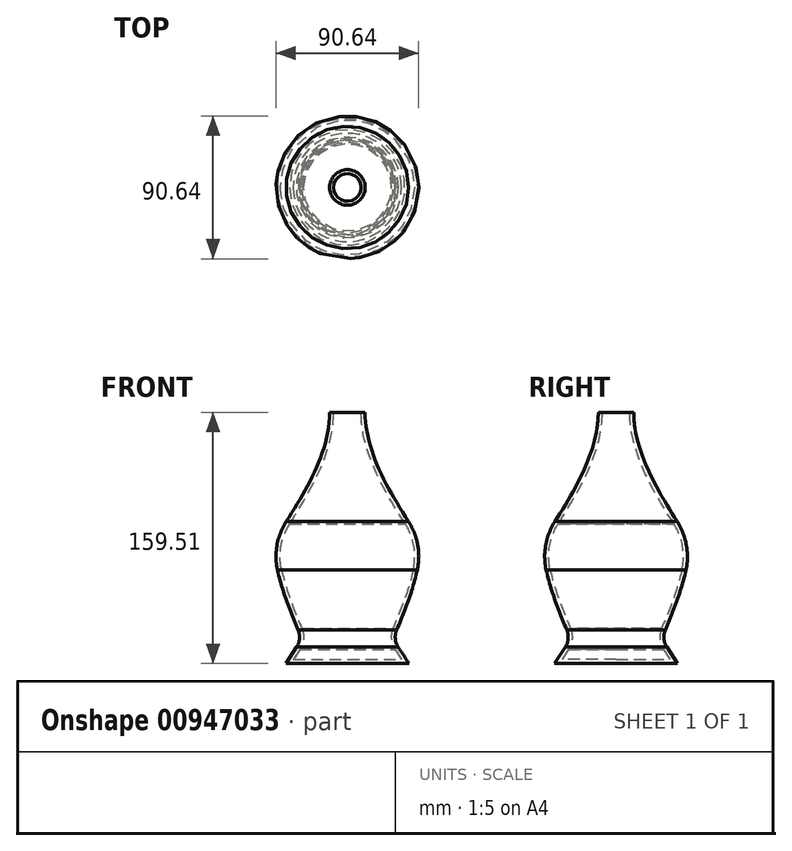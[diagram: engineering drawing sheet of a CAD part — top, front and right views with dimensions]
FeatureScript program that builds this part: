
annotation { "Feature Type Name" : "Feature", "Feature Type Description" : "" }
export const myFeature = defineFeature(function(context is Context, id is Id, definition is map)
    precondition{}
    {
        {
            var Q0;
            Q0=qCreatedBy(makeId("Top.planeOp"),FACE);
            cPlane(context, id + "F0", {"entities" : qUnion([Q0]), "cplaneType" : CPlaneType.OFFSET, "offset" : 62.74 * mm, "oppositeDirection" : true, "width" : 152.4 * mm, "height" : 152.4 * mm});
        }
        {
            var Q0;
            Q0=qCreatedBy(id+"F0.planeOp",FACE);
            cPlane(context, id + "F1", {"entities" : qUnion([Q0]), "cplaneType" : CPlaneType.OFFSET, "offset" : 15.5 * mm, "oppositeDirection" : true, "width" : 152.4 * mm, "height" : 152.4 * mm});
        }
        {
            var Q0;
            Q0=qCreatedBy(id+"F0.planeOp",FACE);
            var sketch = newSketch(context, id + "F2", { "sketchPlane" : qUnion([Q0])});
            skCircle(sketch, "E0", {"center": v(0, 0) * mm, "radius": 28.87 * mm});
            skSolve(sketch);
        }
        {
            var Q0;
            Q0=qCreatedBy(makeId("Top.planeOp"),FACE);
            var sketch = newSketch(context, id + "F3", { "sketchPlane" : qUnion([Q0])});
            skCircle(sketch, "E1", {"center": v(0, 0) * mm, "radius": 46.55 * mm});
            skSolve(sketch);
        }
        {
            var Q0;
            Q0=qCreatedBy(makeId("Top.planeOp"),FACE);
            cPlane(context, id + "F4", {"entities" : qUnion([Q0]), "cplaneType" : CPlaneType.OFFSET, "offset" : 81.28 * mm, "width" : 152.4 * mm, "height" : 152.4 * mm});
        }
        {
            var Q0;
            Q0=qCreatedBy(id+"F4.planeOp",FACE);
            var sketch = newSketch(context, id + "F5", { "sketchPlane" : qUnion([Q0])});
            skCircle(sketch, "E2", {"center": v(0, 0) * mm, "radius": 11.28 * mm});
            skSolve(sketch);
        }
        {
            var Q0;
            Q0=makeQuery(id+"F5.imprint","IMPRINT",FACE,{"disambiguationData":[TD([[makeQuery(id+"F5.imprint","IMPRINT",EDGE,{"derivedFrom":sQuery(id+"F5.wireOp",EDGE,"E2")}),1.0]])]});
            var Q1;
            Q1=makeQuery(id+"F3.imprint","IMPRINT",FACE,{"disambiguationData":[TD([[makeQuery(id+"F3.imprint","IMPRINT",EDGE,{"derivedFrom":sQuery(id+"F3.wireOp",EDGE,"E1")}),1.0]])]});
            loft(context, id + "F6", {"startCondition" : LoftEndDerivativeType.NORMAL_TO_PROFILE, "startMagnitude" : 1, "sheetProfilesArray" : [{ "sheetProfileEntities" : qUnion([Q0]) }, { "sheetProfileEntities" : qUnion([Q1]) }]});
        }
        {
            var Q1;
            Q1=makeQuery(id+"F6.opLoft","CAP_FACE",FACE,{"disambiguationData":[OSD([makeQuery(id+"F3.imprint","IMPRINT",FACE,{"disambiguationData":[TD([[makeQuery(id+"F3.imprint","IMPRINT",EDGE,{"derivedFrom":sQuery(id+"F3.wireOp",EDGE,"E1")}),1.0]])]})])],"isStart":true});
            var Q2;
            Q2=makeQuery(id+"F2.imprint","IMPRINT",FACE,{"disambiguationData":[TD([[makeQuery(id+"F2.imprint","IMPRINT",EDGE,{"derivedFrom":sQuery(id+"F2.wireOp",EDGE,"E0")}),1.0]])]});
            loft(context, id + "F7", {"operationType" : NewBodyOperationType.ADD, "startCondition" : LoftEndDerivativeType.NORMAL_TO_PROFILE, "startMagnitude" : 1, "sheetProfilesArray" : [{ "sheetProfileEntities" : qUnion([Q1]) }, { "sheetProfileEntities" : qUnion([Q2]) }]});
        }
        {
            var Q0;
            Q0=qCreatedBy(id+"F1.planeOp",FACE);
            var sketch = newSketch(context, id + "F8", { "sketchPlane" : qUnion([Q0])});
            skCircle(sketch, "E3", {"center": v(0, 0) * mm, "radius": 39.12 * mm});
            skSolve(sketch);
        }
        {
            var Q1;
            Q1=makeQuery(id+"F8.imprint","IMPRINT",FACE,{"disambiguationData":[TD([[makeQuery(id+"F8.imprint","IMPRINT",EDGE,{"derivedFrom":sQuery(id+"F8.wireOp",EDGE,"E3")}),1.0]])]});
            var Q2;
            Q2=makeQuery(id+"F7.opLoft","CAP_FACE",FACE,{"disambiguationData":[OSD([makeQuery(id+"F2.imprint","IMPRINT",FACE,{"disambiguationData":[TD([[makeQuery(id+"F2.imprint","IMPRINT",EDGE,{"derivedFrom":sQuery(id+"F2.wireOp",EDGE,"E0")}),1.0]])]})])],"isStart":true});
            loft(context, id + "F9", {"operationType" : NewBodyOperationType.ADD, "sheetProfilesArray" : [{ "sheetProfileEntities" : qUnion([Q1]) }, { "sheetProfileEntities" : qUnion([Q2]) }]});
        }
        {
            var Q0;
            {var subQ0=sQuery(id+"F2.wireOp",EDGE,"E0");Q0=makeQuery(id+"F9.boolean.opBoolean","MERGE",EDGE,{"derivedFrom":[makeQuery(id+"F7.opLoft","MID_CAP_EDGE",EDGE,{"disambiguationData":[OSD([subQ0])],"capPos":1.0}),makeQuery(id+"F9.opLoft","MID_CAP_EDGE",EDGE,{"disambiguationData":[OSD([subQ0])],"capPos":1.0})]});}
            fillet(context, id + "F10", {"entities" : qUnion([Q0]), "radius" : 11.54 * mm, "tangentPropagation" : true, "allowEdgeOverflow" : false});
        }
        {
            var Q0;
            {var subQ0=sQuery(id+"F3.wireOp",EDGE,"E1");Q0=makeQuery(id+"F7.boolean.opBoolean","MERGE",EDGE,{"derivedFrom":[makeQuery(id+"F6.opLoft","MID_CAP_EDGE",EDGE,{"disambiguationData":[OSD([subQ0])],"capPos":1.0}),makeQuery(id+"F7.opLoft","MID_CAP_EDGE",EDGE,{"disambiguationData":[OSD([subQ0])],"capPos":0.0})]});}
            fillet(context, id + "F11", {"entities" : qUnion([Q0]), "radius" : 40.93 * mm, "tangentPropagation" : true, "allowEdgeOverflow" : false});
        }
        {
            var Q0;
            Q0=makeQuery(id+"F6.opLoft","CAP_FACE",FACE,{"disambiguationData":[OSD([makeQuery(id+"F5.imprint","IMPRINT",FACE,{"disambiguationData":[TD([[makeQuery(id+"F5.imprint","IMPRINT",EDGE,{"derivedFrom":sQuery(id+"F5.wireOp",EDGE,"E2")}),1.0]])]})])],"isStart":true});
            shell(context, id + "F12", {"entities" : qUnion([Q0]), "thickness" : 2.54 * mm});
        }
    });
